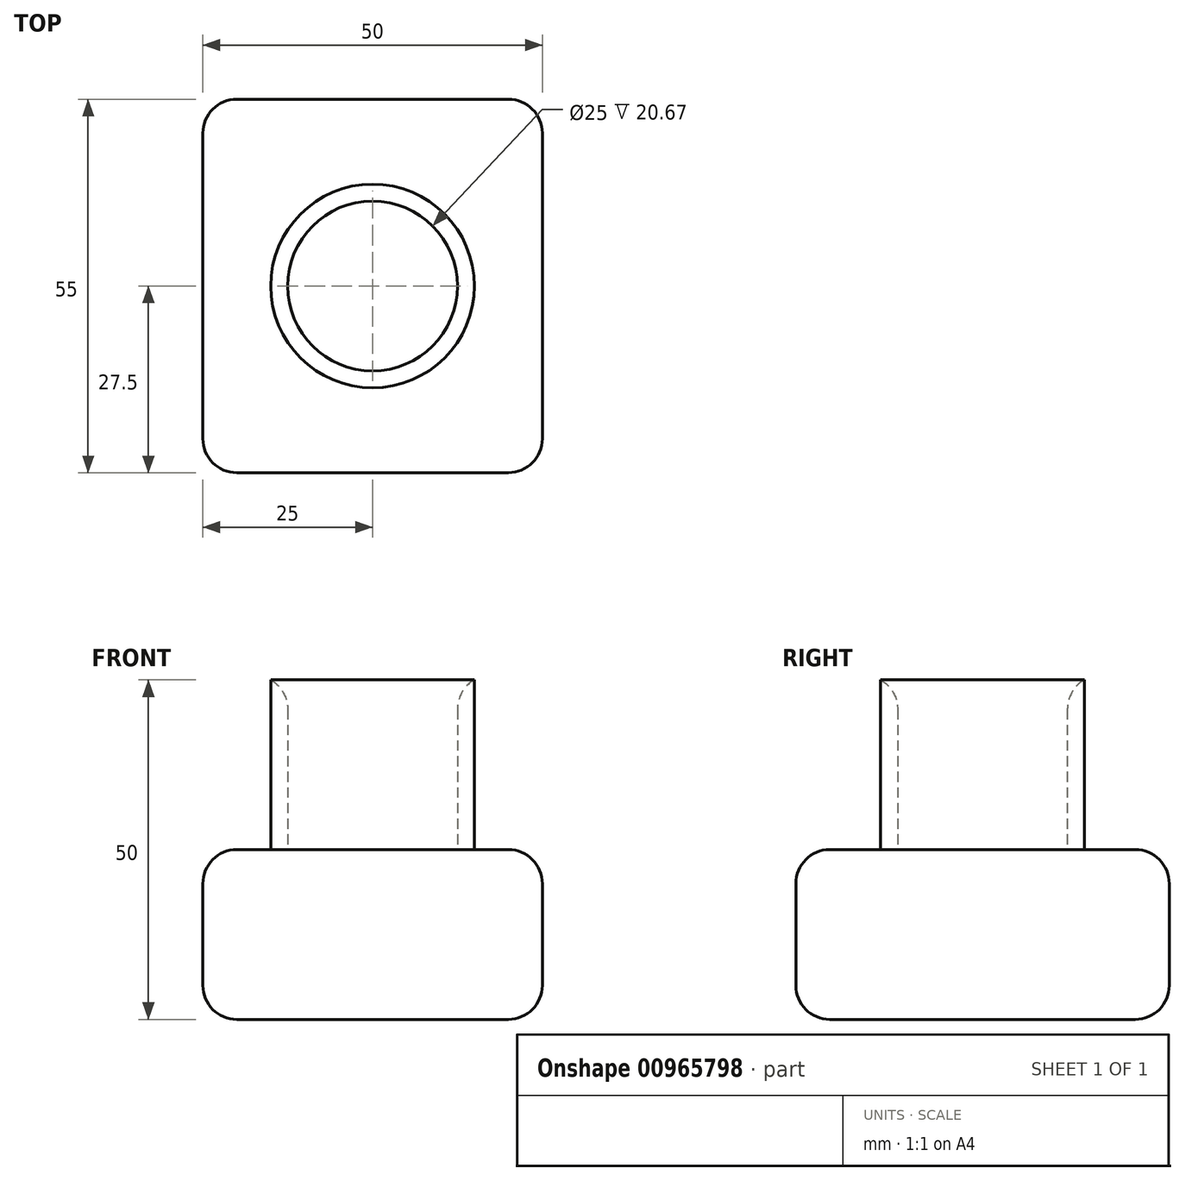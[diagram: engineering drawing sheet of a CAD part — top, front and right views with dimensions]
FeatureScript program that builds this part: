
annotation { "Feature Type Name" : "Feature", "Feature Type Description" : "" }
export const myFeature = defineFeature(function(context is Context, id is Id, definition is map)
    precondition{}
    {
        {
            var Q0;
            Q0=qCreatedBy(makeId("Top.planeOp"),FACE);
            var sketch = newSketch(context, id + "F0", { "sketchPlane" : qUnion([Q0])});
            skLineSegment(sketch, "E0.bottom", {"start": v(-50, 55) * mm, "end": v(0, 55) * mm});
            skLineSegment(sketch, "E0.top", {"start": v(-50, 0) * mm, "end": v(0, 0) * mm});
            skLineSegment(sketch, "E0.left", {"start": v(-50, 55) * mm, "end": v(-50, 0) * mm});
            skLineSegment(sketch, "E0.right", {"start": v(0, 55) * mm, "end": v(0, 0) * mm});
            skCircle(sketch, "E1", {"center": v(-25, 27.5) * mm, "radius": 15 * mm});
            skCircle(sketch, "E2", {"center": v(-25, 27.5) * mm, "radius": 12.5 * mm});
            skSolve(sketch);
        }
        {
            var Q0;
            Q0=makeQuery(id+"F0.imprint","IMPRINT",FACE,{"disambiguationData":[TD([[makeQuery(id+"F0.imprint","IMPRINT",EDGE,{"derivedFrom":sQuery(id+"F0.wireOp",EDGE,"E0.bottom")}),-1.0]])]});
            var Q1;
            Q1=makeQuery(id+"F0.imprint","IMPRINT",FACE,{"disambiguationData":[TD([[makeQuery(id+"F0.imprint","IMPRINT",EDGE,{"derivedFrom":sQuery(id+"F0.wireOp",EDGE,"E2")}),1.0]])]});
            var Q2;
            Q2=makeQuery(id+"F0.imprint","IMPRINT",FACE,{"disambiguationData":[TD([[makeQuery(id+"F0.imprint","IMPRINT",EDGE,{"derivedFrom":sQuery(id+"F0.wireOp",EDGE,"E1")}),1.0]])]});
            extrude(context, id + "F1", {"entities" : qUnion([Q0, Q1, Q2]), "depth" : 25 * mm, "offsetDistance" : 25 * mm});
        }
        {
            var Q0;
            Q0=makeQuery(id+"F0.imprint","IMPRINT",FACE,{"disambiguationData":[TD([[makeQuery(id+"F0.imprint","IMPRINT",EDGE,{"derivedFrom":sQuery(id+"F0.wireOp",EDGE,"E1")}),1.0]])]});
            extrude(context, id + "F2", {"entities" : qUnion([Q0]), "operationType" : NewBodyOperationType.ADD, "depth" : 50 * mm, "offsetDistance" : 25 * mm});
        }
        {
            var Q0;
            Q0=makeQuery(id+"F2.opExtrude","CAP_EDGE",EDGE,{"disambiguationData":[OSD([sQuery(id+"F0.wireOp",EDGE,"E2")])],"isStart":false});
            var Q1;
            Q1=makeQuery(id+"F1.opExtrude","CAP_EDGE",EDGE,{"disambiguationData":[OSD([sQuery(id+"F0.wireOp",EDGE,"E0.bottom")])],"isStart":false});
            var Q2;
            Q2=makeQuery(id+"F1.opExtrude","CAP_EDGE",EDGE,{"disambiguationData":[OSD([sQuery(id+"F0.wireOp",EDGE,"E0.left")])],"isStart":false});
            var Q3;
            Q3=makeQuery(id+"F1.opExtrude","SWEPT_FACE",FACE,{"disambiguationData":[OSD([sQuery(id+"F0.wireOp",EDGE,"E0.top")])]});
            var Q4;
            Q4=makeQuery(id+"F1.opExtrude","SWEPT_FACE",FACE,{"disambiguationData":[OSD([sQuery(id+"F0.wireOp",EDGE,"E0.right")])]});
            var Q5;
            Q5=makeQuery(id+"F1.opExtrude","SWEPT_FACE",FACE,{"disambiguationData":[OSD([sQuery(id+"F0.wireOp",EDGE,"E0.bottom")])]});
            var Q6;
            Q6=makeQuery(id+"F1.opExtrude","SWEPT_FACE",FACE,{"disambiguationData":[OSD([sQuery(id+"F0.wireOp",EDGE,"E0.left")])]});
            fillet(context, id + "F3", {"entities" : qUnion([Q0, Q1, Q2, Q3, Q4, Q5, Q6]), "radius" : 5 * mm, "tangentPropagation" : true, "allowEdgeOverflow" : false});
        }
    });
